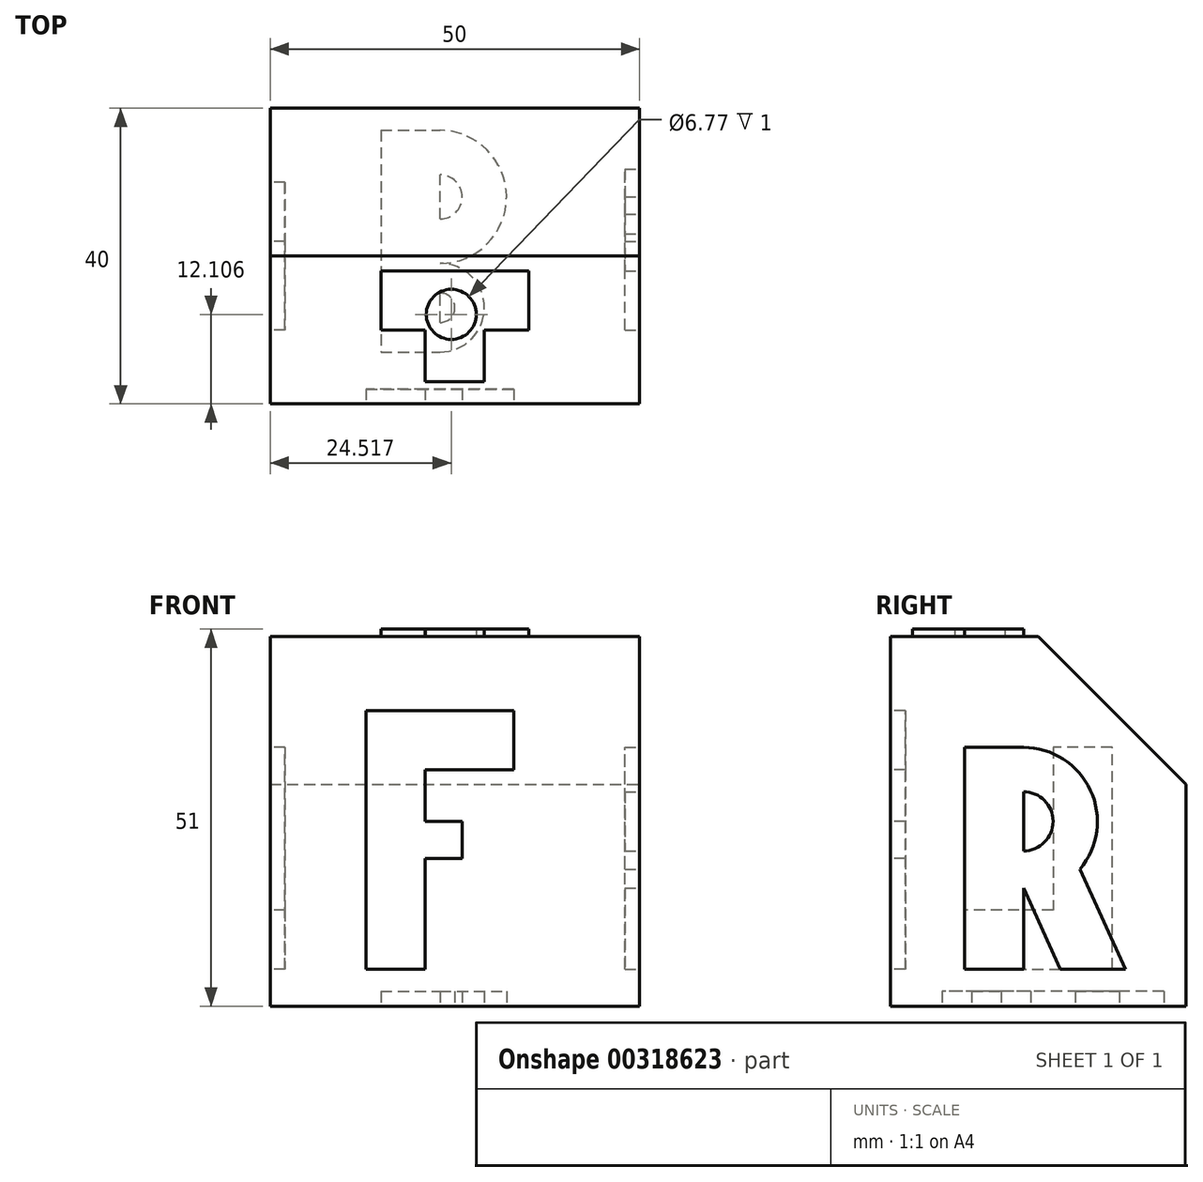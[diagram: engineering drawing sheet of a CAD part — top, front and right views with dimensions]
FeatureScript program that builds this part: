
annotation { "Feature Type Name" : "Feature", "Feature Type Description" : "" }
export const myFeature = defineFeature(function(context is Context, id is Id, definition is map)
    precondition{}
    {
        {
            var Q0;
            Q0=qCreatedBy(makeId("Front.planeOp"),FACE);
            var sketch = newSketch(context, id + "F0", { "sketchPlane" : qUnion([Q0])});
            skLineSegment(sketch, "E0", {"start": v(0, 0) * mm, "end": v(-50, 0) * mm});
            skLineSegment(sketch, "E1", {"start": v(-50, 0) * mm, "end": v(-50, 50) * mm});
            skLineSegment(sketch, "E2", {"start": v(-50, 50) * mm, "end": v(0, 50) * mm});
            skLineSegment(sketch, "E3", {"start": v(0, 50) * mm, "end": v(0, 0) * mm});
            skSolve(sketch);
        }
        {
            var Q0;
            Q0=makeQuery(id+"F0.imprint","IMPRINT",FACE,{"disambiguationData":[TD([[makeQuery(id+"F0.imprint","IMPRINT",EDGE,{"derivedFrom":sQuery(id+"F0.wireOp",EDGE,"E0")}),-1.0]])]});
            extrude(context, id + "F1", {"entities" : qUnion([Q0]), "oppositeDirection" : true, "depth" : 40 * mm});
        }
        {
            var Q0;
            Q0=makeQuery(id+"F1.opExtrude","CAP_EDGE",EDGE,{"disambiguationData":[OSD([sQuery(id+"F0.wireOp",EDGE,"E2")])],"isStart":false});
            chamfer(context, id + "F2", {"entities" : qUnion([Q0]), "width" : 20 * mm, "tangentPropagation" : true});
        }
        {
            var Q0;
            Q0=makeQuery(id+"F1.opExtrude","CAP_FACE",FACE,{"disambiguationData":[OSD([sQuery(id+"F0.wireOp",EDGE,"E0"),sQuery(id+"F0.wireOp",EDGE,"E1"),sQuery(id+"F0.wireOp",EDGE,"E2"),sQuery(id+"F0.wireOp",EDGE,"E3")])],"isStart":true});
            var sketch = newSketch(context, id + "F3", { "sketchPlane" : qUnion([Q0])});
            skLineSegment(sketch, "E4", {"start": v(-50, 5) * mm, "end": v(0, 5) * mm, "construction": true});
            skLineSegment(sketch, "E5", {"start": v(-37, 5) * mm, "end": v(-37, 40) * mm});
            skLineSegment(sketch, "E6", {"start": v(-37, 40) * mm, "end": v(-17, 40) * mm});
            skLineSegment(sketch, "E7", {"start": v(-17, 40) * mm, "end": v(-17, 32) * mm});
            skLineSegment(sketch, "E8", {"start": v(-17, 32) * mm, "end": v(-29, 32) * mm});
            skLineSegment(sketch, "E9", {"start": v(-29, 32) * mm, "end": v(-29, 25) * mm});
            skLineSegment(sketch, "E10", {"start": v(-29, 25) * mm, "end": v(-24, 25) * mm});
            skLineSegment(sketch, "E11", {"start": v(-24, 25) * mm, "end": v(-24, 20) * mm});
            skLineSegment(sketch, "E12", {"start": v(-24, 20) * mm, "end": v(-29, 20) * mm});
            skLineSegment(sketch, "E13", {"start": v(-29, 20) * mm, "end": v(-29, 5) * mm});
            skLineSegment(sketch, "E14", {"start": v(-29, 5) * mm, "end": v(-37, 5) * mm});
            skSolve(sketch);
        }
        {
            var Q0;
            Q0=makeQuery(id+"F3.imprint","IMPRINT",FACE,{"disambiguationData":[TD([[makeQuery(id+"F3.imprint","IMPRINT",EDGE,{"derivedFrom":sQuery(id+"F3.wireOp",EDGE,"E5")}),-1.0]])]});
            extrude(context, id + "F4", {"entities" : qUnion([Q0]), "operationType" : NewBodyOperationType.REMOVE, "oppositeDirection" : true, "depth" : 2 * mm});
        }
        {
            var Q0;
            Q0=makeQuery(id+"F1.opExtrude","SWEPT_FACE",FACE,{"disambiguationData":[OSD([sQuery(id+"F0.wireOp",EDGE,"E3")])]});
            var sketch = newSketch(context, id + "F5", { "sketchPlane" : qUnion([Q0])});
            skLineSegment(sketch, "E15", {"start": v(0, 5) * mm, "end": v(40, 5) * mm, "construction": true});
            skLineSegment(sketch, "E16", {"start": v(10, 5) * mm, "end": v(10, 35) * mm});
            skLineSegment(sketch, "E17", {"start": v(10, 35) * mm, "end": v(18, 35) * mm});
            skLineSegment(sketch, "E18", {"start": v(18, 29) * mm, "end": v(18, 21) * mm});
            skLineSegment(sketch, "E19", {"start": v(18, 5) * mm, "end": v(10, 5) * mm});
            skArc(sketch, "E20", {"start": v(25.63, 18.54) * mm, "mid": v(27.07, 29.2) * mm, "end": v(18, 35) * mm});
            skLineSegment(sketch, "E21", {"start": v(18, 16) * mm, "end": v(23, 5) * mm});
            skLineSegment(sketch, "E22", {"start": v(23, 5) * mm, "end": v(31.79, 5) * mm});
            skLineSegment(sketch, "E23", {"start": v(31.79, 5) * mm, "end": v(25.63, 18.54) * mm});
            skLineSegment(sketch, "E24", {"start": v(20.5, 10.5) * mm, "end": v(27.78, 13.81) * mm, "construction": true});
            skArc(sketch, "E25", {"start": v(18, 21) * mm, "mid": v(22, 25) * mm, "end": v(18, 29) * mm});
            skLineSegment(sketch, "E26.trimOffspring", {"start": v(18, 16) * mm, "end": v(18, 5) * mm});
            skSolve(sketch);
        }
        {
            var Q0;
            Q0=makeQuery(id+"F5.imprint","IMPRINT",FACE,{"disambiguationData":[TD([[makeQuery(id+"F5.imprint","IMPRINT",EDGE,{"derivedFrom":sQuery(id+"F5.wireOp",EDGE,"E16")}),-1.0]])]});
            extrude(context, id + "F6", {"entities" : qUnion([Q0]), "operationType" : NewBodyOperationType.REMOVE, "oppositeDirection" : true, "depth" : 2 * mm});
        }
        {
            var Q0;
            Q0=makeQuery(id+"F1.opExtrude","SWEPT_FACE",FACE,{"disambiguationData":[OSD([sQuery(id+"F0.wireOp",EDGE,"E1")])]});
            var sketch = newSketch(context, id + "F7", { "sketchPlane" : qUnion([Q0])});
            skLineSegment(sketch, "E27", {"start": v(-30, 35) * mm, "end": v(-22, 35) * mm});
            skLineSegment(sketch, "E28", {"start": v(-22, 35) * mm, "end": v(-22, 13) * mm});
            skLineSegment(sketch, "E29", {"start": v(-22, 13) * mm, "end": v(-10, 13) * mm});
            skLineSegment(sketch, "E30", {"start": v(-10, 13) * mm, "end": v(-10, 5) * mm});
            skLineSegment(sketch, "E31", {"start": v(-10, 5) * mm, "end": v(-30, 5) * mm});
            skLineSegment(sketch, "E32", {"start": v(-30, 5) * mm, "end": v(-30, 35) * mm});
            skSolve(sketch);
        }
        {
            var Q0;
            Q0=makeQuery(id+"F7.imprint","IMPRINT",FACE,{"disambiguationData":[TD([[makeQuery(id+"F7.imprint","IMPRINT",EDGE,{"derivedFrom":sQuery(id+"F7.wireOp",EDGE,"E27")}),-1.0]])]});
            extrude(context, id + "F8", {"entities" : qUnion([Q0]), "operationType" : NewBodyOperationType.REMOVE, "oppositeDirection" : true, "depth" : 2 * mm});
        }
        {
            var Q0;
            Q0=makeQuery(id+"F1.opExtrude","SWEPT_FACE",FACE,{"disambiguationData":[OSD([sQuery(id+"F0.wireOp",EDGE,"E2")])]});
            var sketch = newSketch(context, id + "F9", { "sketchPlane" : qUnion([Q0])});
            skLineSegment(sketch, "E33", {"start": v(-29, 3) * mm, "end": v(-29, 10) * mm});
            skLineSegment(sketch, "E34", {"start": v(-29, 10) * mm, "end": v(-35, 10) * mm});
            skLineSegment(sketch, "E35", {"start": v(-35, 10) * mm, "end": v(-35, 18) * mm});
            skLineSegment(sketch, "E36", {"start": v(-35, 18) * mm, "end": v(-15, 18) * mm});
            skLineSegment(sketch, "E37", {"start": v(-15, 18) * mm, "end": v(-15, 10) * mm});
            skLineSegment(sketch, "E38", {"start": v(-15, 10) * mm, "end": v(-21, 10) * mm});
            skLineSegment(sketch, "E39", {"start": v(-21, 10) * mm, "end": v(-21, 3) * mm});
            skLineSegment(sketch, "E40", {"start": v(-21, 3) * mm, "end": v(-29, 3) * mm});
            skCircle(sketch, "E41", {"center": v(-25.48, 12.1) * mm, "radius": 3.39 * mm});
            skSolve(sketch);
        }
        {
            var Q0;
            Q0=makeQuery(id+"F9.imprint","IMPRINT",FACE,{"disambiguationData":[TD([[makeQuery(id+"F9.imprint","IMPRINT",EDGE,{"derivedFrom":sQuery(id+"F9.wireOp",EDGE,"E33")}),-1.0]])]});
            extrude(context, id + "F10", {"entities" : qUnion([Q0]), "operationType" : NewBodyOperationType.ADD, "depth" : 1 * mm});
        }
        {
            var Q0;
            Q0=makeQuery(id+"F1.opExtrude","SWEPT_FACE",FACE,{"disambiguationData":[OSD([sQuery(id+"F0.wireOp",EDGE,"E0")])]});
            var sketch = newSketch(context, id + "F11", { "sketchPlane" : qUnion([Q0])});
            skLineSegment(sketch, "E42", {"start": v(-35, -37) * mm, "end": v(-35, -7) * mm});
            skLineSegment(sketch, "E43", {"start": v(-35, -7) * mm, "end": v(-27, -7) * mm});
            skLineSegment(sketch, "E44", {"start": v(-35, -37) * mm, "end": v(-27, -37) * mm});
            skArc(sketch, "E45", {"start": v(-27, -19) * mm, "mid": v(-21, -13) * mm, "end": v(-27, -7) * mm});
            skArc(sketch, "E46", {"start": v(-27, -37) * mm, "mid": v(-18, -28) * mm, "end": v(-27, -19) * mm});
            skLineSegment(sketch, "E47", {"start": v(-27, -11) * mm, "end": v(-27, -15) * mm});
            skArc(sketch, "E48", {"start": v(-27, -15) * mm, "mid": v(-25, -13) * mm, "end": v(-27, -11) * mm});
            skArc(sketch, "E49", {"start": v(-27, -31) * mm, "mid": v(-24, -28) * mm, "end": v(-27, -25) * mm});
            skLineSegment(sketch, "E50.trimOffspring", {"start": v(-27, -25) * mm, "end": v(-27, -31) * mm});
            skSolve(sketch);
        }
        {
            var Q0;
            Q0=makeQuery(id+"F11.imprint","IMPRINT",FACE,{"disambiguationData":[TD([[makeQuery(id+"F11.imprint","IMPRINT",EDGE,{"derivedFrom":sQuery(id+"F11.wireOp",EDGE,"E42")}),-1.0]])]});
            extrude(context, id + "F12", {"entities" : qUnion([Q0]), "operationType" : NewBodyOperationType.REMOVE, "oppositeDirection" : true, "depth" : 2 * mm});
        }
    });
